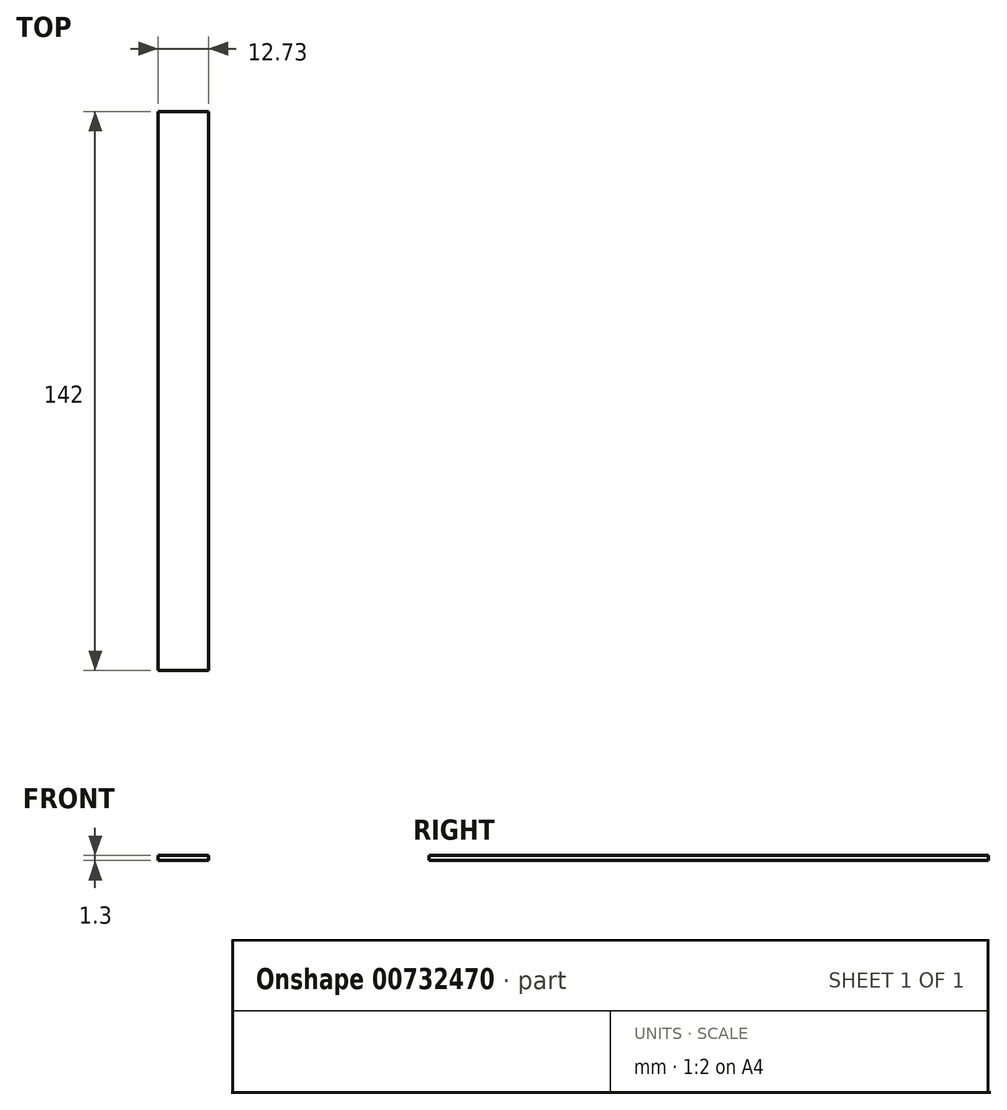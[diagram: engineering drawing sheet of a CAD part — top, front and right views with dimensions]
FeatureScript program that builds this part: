
annotation { "Feature Type Name" : "Feature", "Feature Type Description" : "" }
export const myFeature = defineFeature(function(context is Context, id is Id, definition is map)
    precondition{}
    {
        {
            var Q0;
            Q0=qCreatedBy(makeId("Top.planeOp"),FACE);
            var sketch = newSketch(context, id + "F0", { "sketchPlane" : qUnion([Q0])});
            skLineSegment(sketch, "E0.bottom", {"start": v(-24.87, 81.91) * mm, "end": v(-12.14, 81.91) * mm});
            skLineSegment(sketch, "E0.top", {"start": v(-24.87, -60.09) * mm, "end": v(-12.14, -60.09) * mm});
            skLineSegment(sketch, "E0.left", {"start": v(-24.87, 81.91) * mm, "end": v(-24.87, -60.09) * mm});
            skLineSegment(sketch, "E0.right", {"start": v(-12.14, 81.91) * mm, "end": v(-12.14, -60.09) * mm});
            skSolve(sketch);
        }
        {
            var Q0;
            Q0 = qSketchRegion(id + "F0", true);
            extrude(context, id + "F1", {"entities" : qUnion([Q0]), "depth" : 1.3 * mm, "offsetDistance" : 25.4 * mm});
        }
    });
